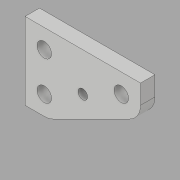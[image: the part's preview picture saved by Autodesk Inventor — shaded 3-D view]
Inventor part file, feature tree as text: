
AUTODESK INVENTOR PART (.ipt)
format: ipt  version: 2020 (Build 240168000, 168)  size: 118,272 bytes
history: native  units: in
note: dims shown in document units (in); Inventor stores cm internally (conversion verified against a paired STEP export)
features: extrude x1, sketch x1
ambient origin geometry x8: Origin, YZ Plane, XZ Plane, XY Plane, X Axis, Y Axis, Z Axis, Center Point
bodies: Solid1 (feature_tree)
feature tree (2):
  extrude  "Extrusion1"  Depth=0.5in
  sketch  "Sketch1"  dims[d2=2.0in d3=0.5in d4=0.5in d5=0.5in d7=0.378in d8=1.0in d10=2.0in d11=0.5in d12=0.25in d13=0.5in d14=1.0in d15=0.5in d16=3.0in d17=0.375in d18=0.0in]
